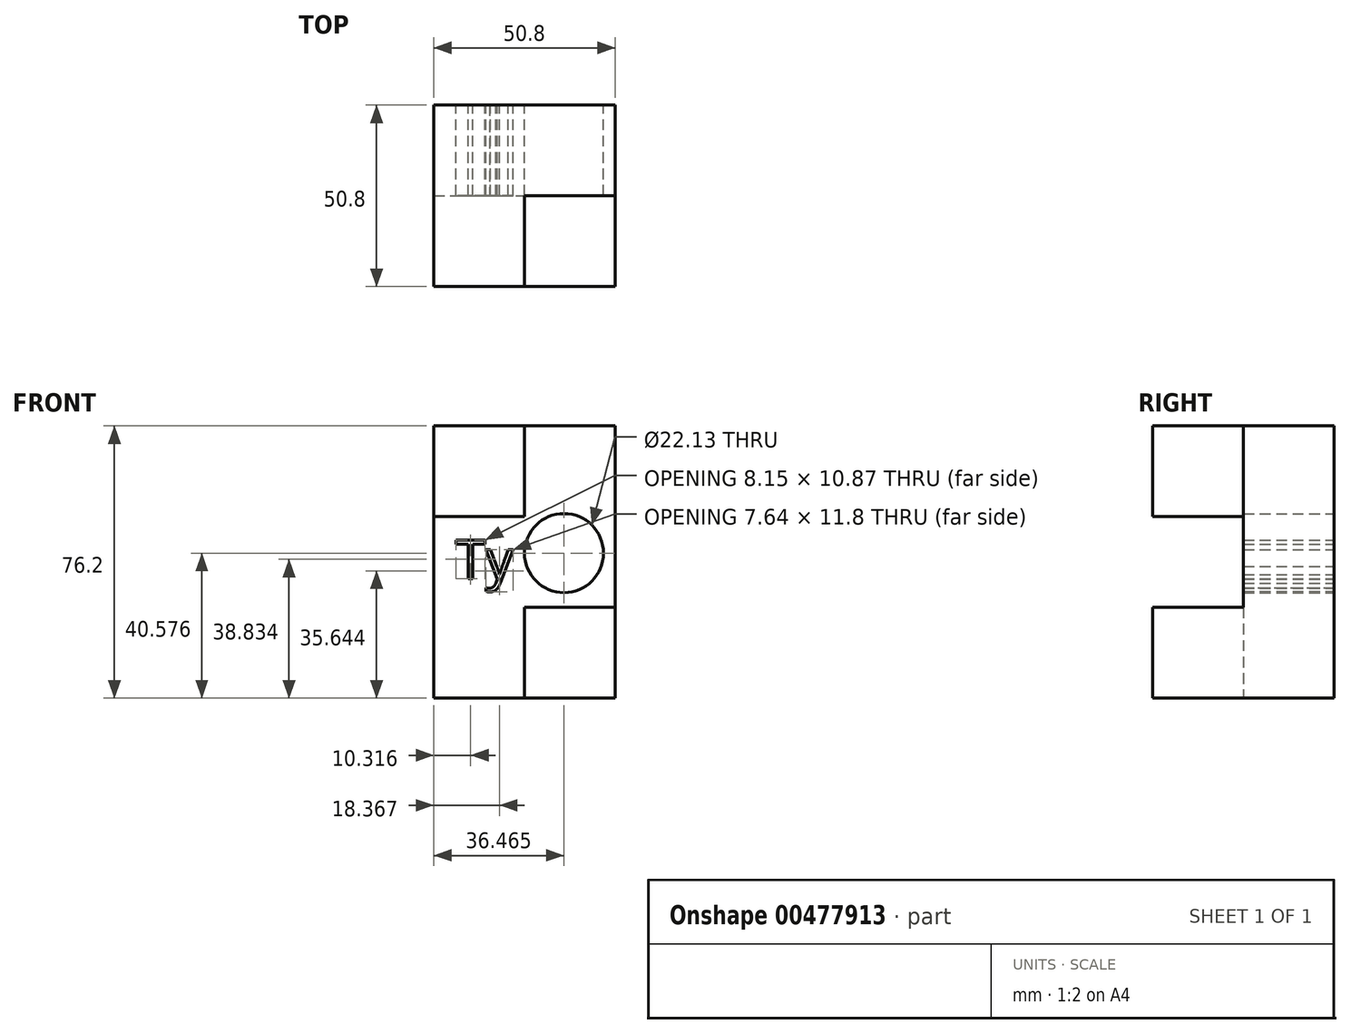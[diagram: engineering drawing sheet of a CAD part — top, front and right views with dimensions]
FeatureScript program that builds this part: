
annotation { "Feature Type Name" : "Feature", "Feature Type Description" : "" }
export const myFeature = defineFeature(function(context is Context, id is Id, definition is map)
    precondition{}
    {
        {
            var Q0;
            Q0=qCreatedBy(makeId("Front.planeOp"),FACE);
            var sketch = newSketch(context, id + "F0", { "sketchPlane" : qUnion([Q0])});
            skLineSegment(sketch, "E0.bottom", {"start": v(25.4, 0) * mm, "end": v(50.8, 0) * mm});
            skLineSegment(sketch, "E0.top", {"start": v(25.4, -25.4) * mm, "end": v(50.8, -25.4) * mm});
            skLineSegment(sketch, "E0.right", {"start": v(50.8, 0) * mm, "end": v(50.8, -25.4) * mm});
            skLineSegment(sketch, "E1", {"start": v(25.4, 0) * mm, "end": v(25.4, -25.4) * mm});
            skSolve(sketch);
        }
        {
            var Q0;
            Q0=makeQuery(id+"F0.imprint","IMPRINT",FACE,{"disambiguationData":[TD([[makeQuery(id+"F0.imprint","IMPRINT",EDGE,{"derivedFrom":sQuery(id+"F0.wireOp",EDGE,"E0.bottom")}),-1.0]])]});
            extrude(context, id + "F1", {"entities" : qUnion([Q0]), "depth" : 50.8 * mm});
        }
        {
            var Q0;
            Q0=qCreatedBy(makeId("Front.planeOp"),FACE);
            var sketch = newSketch(context, id + "F2", { "sketchPlane" : qUnion([Q0])});
            skLineSegment(sketch, "E2.top", {"start": v(0, -25.4) * mm, "end": v(25.4, -25.4) * mm});
            skLineSegment(sketch, "E2.left", {"start": v(0, 0) * mm, "end": v(0, -25.4) * mm});
            skLineSegment(sketch, "E2.right", {"start": v(25.4, 0) * mm, "end": v(25.4, -25.4) * mm});
            skLineSegment(sketch, "E3.left", {"start": v(0, 0) * mm, "end": v(0, 25.4) * mm});
            skLineSegment(sketch, "E3.right", {"start": v(50.8, 0) * mm, "end": v(50.8, 25.4) * mm});
            skLineSegment(sketch, "E4.top", {"start": v(50.8, 50.8) * mm, "end": v(25.4, 50.8) * mm});
            skLineSegment(sketch, "E4.left", {"start": v(50.8, 25.4) * mm, "end": v(50.8, 50.8) * mm});
            skLineSegment(sketch, "E4.right", {"start": v(25.4, 25.4) * mm, "end": v(25.4, 50.8) * mm});
            skLineSegment(sketch, "E5", {"start": v(25.4, 25.4) * mm, "end": v(0, 25.4) * mm});
            skLineSegment(sketch, "E6", {"start": v(25.4, 0) * mm, "end": v(50.8, 0) * mm});
            skCircle(sketch, "E7", {"center": v(36.46, 15.18) * mm, "radius": 11.06 * mm});
            skText(sketch, "E8", { "text": "Ty", "fontName": "OpenSans-Regular.ttf"});
            const initialGuessF2  = {"E8": [0.00611, 0.008, 1, 0, 0.01096]};
            skSetInitialGuess(sketch, initialGuessF2);
            skSolve(sketch);
        }
        {
            var Q0;
            Q0=makeQuery(id+"F2.imprint","IMPRINT",FACE,{"disambiguationData":[TD([[makeQuery(id+"F2.imprint","IMPRINT",EDGE,{"derivedFrom":sQuery(id+"F2.wireOp",EDGE,"E2.top")}),1.0]])]});
            extrude(context, id + "F3", {"entities" : qUnion([Q0]), "operationType" : NewBodyOperationType.ADD, "depth" : 25.4 * mm});
        }
        {
            var Q0;
            Q0=qCreatedBy(makeId("Front.planeOp"),FACE);
            var sketch = newSketch(context, id + "F4", { "sketchPlane" : qUnion([Q0])});
            skLineSegment(sketch, "E9.bottom", {"start": v(0, 25.4) * mm, "end": v(25.4, 25.4) * mm});
            skLineSegment(sketch, "E9.top", {"start": v(0, 50.8) * mm, "end": v(25.4, 50.8) * mm});
            skLineSegment(sketch, "E9.left", {"start": v(0, 25.4) * mm, "end": v(0, 50.8) * mm});
            skLineSegment(sketch, "E10", {"start": v(25.4, 50.8) * mm, "end": v(25.4, 25.4) * mm});
            skSolve(sketch);
        }
        {
            var Q0;
            Q0=makeQuery(id+"F4.imprint","IMPRINT",FACE,{"disambiguationData":[TD([[makeQuery(id+"F4.imprint","IMPRINT",EDGE,{"derivedFrom":sQuery(id+"F4.wireOp",EDGE,"E9.bottom")}),1.0]])]});
            extrude(context, id + "F5", {"entities" : qUnion([Q0]), "operationType" : NewBodyOperationType.ADD, "depth" : 50.8 * mm});
        }
    });
